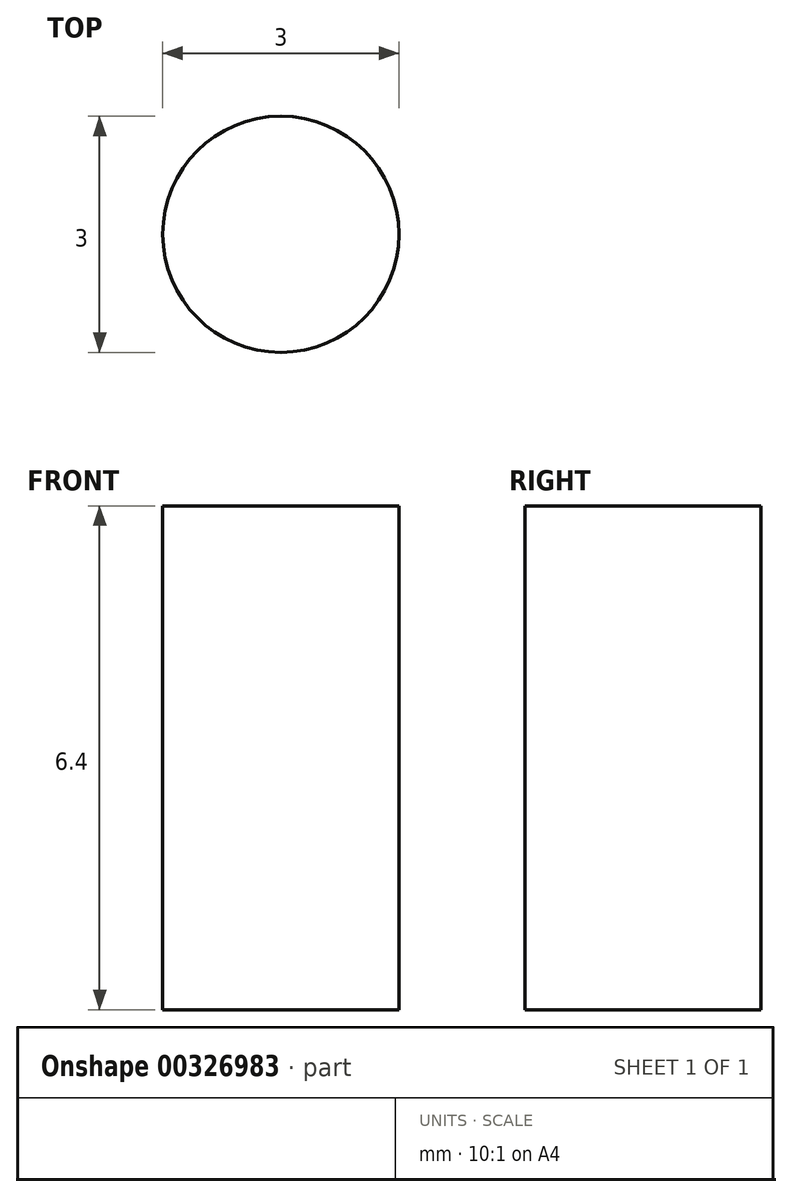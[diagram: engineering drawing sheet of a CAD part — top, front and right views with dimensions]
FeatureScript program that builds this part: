
annotation { "Feature Type Name" : "Feature", "Feature Type Description" : "" }
export const myFeature = defineFeature(function(context is Context, id is Id, definition is map)
    precondition{}
    {
        {
            var Q0;
            Q0=qCreatedBy(makeId("Top.planeOp"),FACE);
            var sketch = newSketch(context, id + "F0", { "sketchPlane" : qUnion([Q0])});
            skCircle(sketch, "E0", {"center": v(0, 0) * mm, "radius": 1.5 * mm});
            skSolve(sketch);
        }
        {
            var Q0;
            Q0 = qSketchRegion(id + "F0", true);
            extrude(context, id + "F1", {"entities" : qUnion([Q0]), "depth" : 3.2 * mm, "hasSecondDirection" : true, "secondDirectionOppositeDirection" : true, "secondDirectionDepth" : 3.2 * mm});
        }
    });
